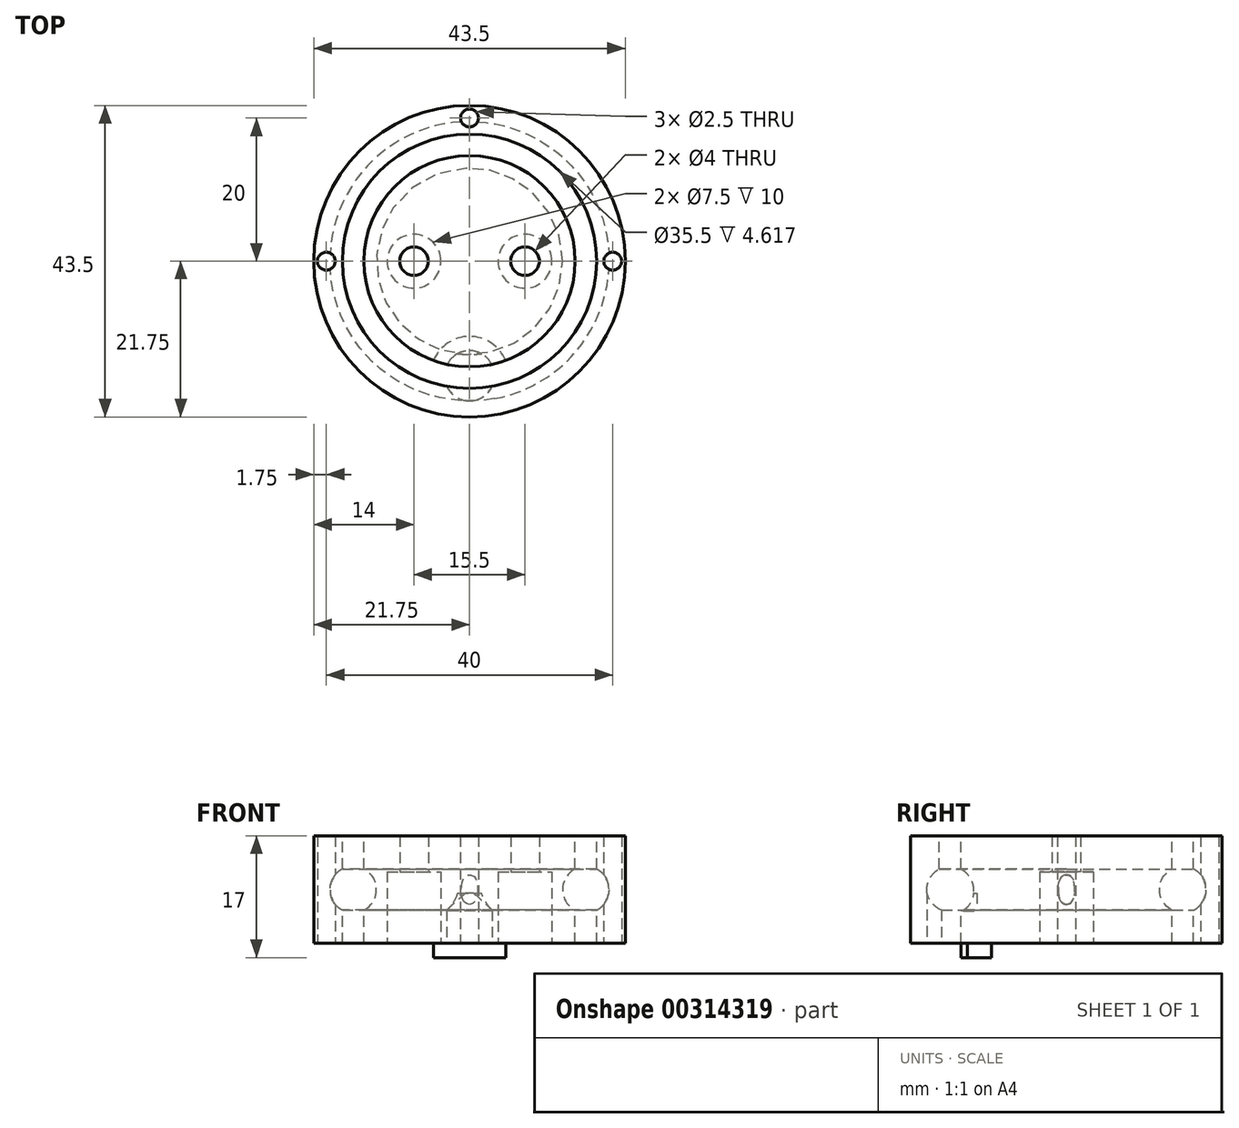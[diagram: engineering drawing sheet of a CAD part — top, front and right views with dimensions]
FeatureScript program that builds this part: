
annotation { "Feature Type Name" : "Feature", "Feature Type Description" : "" }
export const myFeature = defineFeature(function(context is Context, id is Id, definition is map)
    precondition{}
    {
        {
            var Q0;
            Q0=qCreatedBy(makeId("Top.planeOp"),FACE);
            var sketch = newSketch(context, id + "F0", { "sketchPlane" : qUnion([Q0])});
            skCircle(sketch, "E0", {"center": v(0, 0) * mm, "radius": 4 * mm});
            skCircle(sketch, "E1", {"center": v(0, 0) * mm, "radius": 21.75 * mm});
            skCircle(sketch, "E2", {"center": v(0, 0) * mm, "radius": 14.75 * mm});
            skCircle(sketch, "E3", {"center": v(0, 0) * mm, "radius": 17.75 * mm});
            skPoint(sketch, "E4", {"position": v(0, 50.94) * mm});
            skSolve(sketch);
        }
        {
            var Q0;
            Q0=makeQuery(id+"F0.imprint","IMPRINT",FACE,{"disambiguationData":[TD([[makeQuery(id+"F0.imprint","IMPRINT",EDGE,{"derivedFrom":sQuery(id+"F0.wireOp",EDGE,"E1")}),1.0]])]});
            var Q1;
            Q1=makeQuery(id+"F0.imprint","IMPRINT",FACE,{"disambiguationData":[TD([[makeQuery(id+"F0.imprint","IMPRINT",EDGE,{"derivedFrom":sQuery(id+"F0.wireOp",EDGE,"E0")}),-1.0]])]});
            var Q2;
            Q2=makeQuery(id+"F0.imprint","IMPRINT",FACE,{"disambiguationData":[TD([[makeQuery(id+"F0.imprint","IMPRINT",EDGE,{"derivedFrom":sQuery(id+"F0.wireOp",EDGE,"E0")}),1.0]])]});
            extrude(context, id + "F1", {"entities" : qUnion([Q0, Q1, Q2]), "oppositeDirection" : true, "depth" : 15 * mm});
        }
        {
            var Q0;
            Q0=qCreatedBy(makeId("Right.planeOp"),FACE);
            var sketch = newSketch(context, id + "F2", { "sketchPlane" : qUnion([Q0])});
            skLineSegment(sketch, "E5", {"start": v(0, -15) * mm, "end": v(0, 0) * mm});
            skPoint(sketch, "E6", {"position": v(0, -7.5) * mm});
            skSolve(sketch);
        }
        {
            var Q0;
            Q0=makeQuery(id+"F1.opExtrude","CAP_FACE",FACE,{"disambiguationData":[OSD([sQuery(id+"F0.wireOp",EDGE,"E0"),sQuery(id+"F0.wireOp",EDGE,"E2")])],"isStart":false});
            var sketch = newSketch(context, id + "F3", { "sketchPlane" : qUnion([Q0])});
            skPoint(sketch, "E7", {"position": v(0, -14.75) * mm});
            skPoint(sketch, "E8", {"position": v(0, -17.75) * mm});
            skSolve(sketch);
        }
        {
            var Q0;
            Q0=qCreatedBy(makeId("Right.planeOp"),FACE);
            var sketch = newSketch(context, id + "F4", { "sketchPlane" : qUnion([Q0])});
            skCircle(sketch, "E9", {"center": v(16.25, -7.5) * mm, "radius": 3.25 * mm});
            skLineSegment(sketch, "E10", {"start": v(17.75, 0) * mm, "end": v(17.75, -15) * mm});
            skSolve(sketch);
        }
        {
            var Q0;
            Q0=qCreatedBy(makeId("Right.planeOp"),FACE);
            var sketch = newSketch(context, id + "F5", { "sketchPlane" : qUnion([Q0])});
            skLineSegment(sketch, "E11", {"start": v(16.25, -3) * mm, "end": v(16.25, -12) * mm});
            skPoint(sketch, "E12", {"position": v(0, 5) * mm});
            skPoint(sketch, "E13", {"position": v(16.25, -7.5) * mm});
            skArc(sketch, "E14", {"start": v(16.25, -3) * mm, "mid": v(11.75, -7.5) * mm, "end": v(16.25, -12) * mm});
            skSolve(sketch);
        }
        {
            var Q0;
            Q0=makeQuery(id+"F4.imprint","IMPRINT",FACE,{"disambiguationData":[TD([[makeQuery(id+"F4.imprint","IMPRINT",EDGE,{"derivedFrom":sQuery(id+"F4.wireOp",EDGE,"E9")}),1.0]])]});
            var Q1;
            Q1=makeQuery(id+"F1.opExtrude","SWEPT_FACE",FACE,{"disambiguationData":[OSD([sQuery(id+"F0.wireOp",EDGE,"E2")])]});
            revolve(context, id + "F6", {"operationType" : NewBodyOperationType.REMOVE, "entities" : qUnion([Q0]), "axis" : qUnion([Q1]), "revolveType" : RevolveType.FULL, "oppositeDirection" : true});
        }
        {
            var Q0;
            Q0=qCreatedBy(makeId("Top.planeOp"),FACE);
            cPlane(context, id + "F7", {"entities" : qUnion([Q0]), "cplaneType" : CPlaneType.OFFSET, "offset" : 5 * mm, "width" : 150 * mm, "height" : 150 * mm});
        }
        {
            var Q0;
            Q0=makeQuery(id+"F1.opExtrude","CAP_FACE",FACE,{"disambiguationData":[OSD([sQuery(id+"F0.wireOp",EDGE,"E1"),sQuery(id+"F0.wireOp",EDGE,"E3")])],"isStart":false});
            var sketch = newSketch(context, id + "F8", { "sketchPlane" : qUnion([Q0])});
            skCircle(sketch, "E15", {"center": v(0, 16) * mm, "radius": 3.5 * mm});
            skSolve(sketch);
        }
        {
            var Q0;
            Q0=makeQuery(id+"F8.imprint","IMPRINT",FACE,{"disambiguationData":[TD([[makeQuery(id+"F8.imprint","IMPRINT",EDGE,{"derivedFrom":sQuery(id+"F8.wireOp",EDGE,"E15")}),1.0]])]});
            extrude(context, id + "F9", {"entities" : qUnion([Q0]), "operationType" : NewBodyOperationType.REMOVE, "oppositeDirection" : true, "depth" : 7 * mm});
        }
        {
            var Q0;
            Q0=makeQuery(id+"F1.opExtrude","CAP_FACE",FACE,{"disambiguationData":[OSD([sQuery(id+"F0.wireOp",EDGE,"E0"),sQuery(id+"F0.wireOp",EDGE,"E2")])],"isStart":false});
            var sketch = newSketch(context, id + "F10", { "sketchPlane" : qUnion([Q0])});
            skPoint(sketch, "E16", {"position": v(-7.75, 0) * mm});
            skPoint(sketch, "E17", {"position": v(7.75, 0) * mm});
            skCircle(sketch, "E18", {"center": v(-7.75, 0) * mm, "radius": 3.75 * mm});
            skCircle(sketch, "E19", {"center": v(7.75, 0) * mm, "radius": 3.75 * mm});
            skSolve(sketch);
        }
        {
            var Q0;
            Q0=sQuery(id+"F10.wireOp",VERTEX,"E16");
            var Q1;
            Q1=sQuery(id+"F10.wireOp",VERTEX,"E17");
            var Q2;
            Q2=makeQuery(id+"F1.opExtrude","SWEPT_BODY",BODY,{"disambiguationData":[OSD([sQuery(id+"F0.wireOp",EDGE,"E0"),sQuery(id+"F0.wireOp",EDGE,"E2")])]});
            hole(context, id + "F11", {"style" : HoleStyle.SIMPLE, "endStyle" : HoleEndStyle.THROUGH, "holeDiameter" : 4 * mm, "tappedDepth" : 12 * mm, "tapClearance" : 3, "locations" : qUnion([Q0, Q1]), "scope" : qUnion([Q2])});
        }
        {
            var Q0;
            Q0=makeQuery(id+"F10.imprint","IMPRINT",FACE,{"disambiguationData":[TD([[makeQuery(id+"F10.imprint","IMPRINT",EDGE,{"derivedFrom":sQuery(id+"F10.wireOp",EDGE,"E18")}),1.0]])]});
            var Q1;
            Q1=makeQuery(id+"F10.imprint","IMPRINT",FACE,{"disambiguationData":[TD([[makeQuery(id+"F10.imprint","IMPRINT",EDGE,{"derivedFrom":sQuery(id+"F10.wireOp",EDGE,"E19")}),1.0]])]});
            extrude(context, id + "F12", {"entities" : qUnion([Q0, Q1]), "operationType" : NewBodyOperationType.REMOVE, "oppositeDirection" : true, "depth" : 10 * mm});
        }
        {
            var Q0;
            Q0=makeQuery(id+"F1.opExtrude","CAP_FACE",FACE,{"disambiguationData":[OSD([sQuery(id+"F0.wireOp",EDGE,"E1"),sQuery(id+"F0.wireOp",EDGE,"E3")])],"isStart":false});
            var sketch = newSketch(context, id + "F13", { "sketchPlane" : qUnion([Q0])});
            skPoint(sketch, "E20", {"position": v(-20, 0) * mm});
            skPoint(sketch, "E21.1.0", {"position": v(0, -20) * mm});
            skPoint(sketch, "E21.2.0", {"position": v(20, 0) * mm});
            skPoint(sketch, "E21.3.0", {"position": v(0, 20) * mm});
            skPoint(sketch, "E21.center", {"position": v(0, 0) * mm});
            skSolve(sketch);
        }
        {
            var Q0;
            Q0=sQuery(id+"F13.wireOp",VERTEX,"E20");
            var Q1;
            Q1=sQuery(id+"F13.wireOp",VERTEX,"E21.1.0");
            var Q2;
            Q2=sQuery(id+"F13.wireOp",VERTEX,"E21.2.0");
            var Q3;
            Q3=makeQuery(id+"F1.opExtrude","SWEPT_BODY",BODY,{"disambiguationData":[OSD([sQuery(id+"F0.wireOp",EDGE,"E1"),sQuery(id+"F0.wireOp",EDGE,"E3")])]});
            hole(context, id + "F14", {"style" : HoleStyle.SIMPLE, "endStyle" : HoleEndStyle.THROUGH, "holeDiameter" : 2.5 * mm, "tappedDepth" : 12 * mm, "tapClearance" : 3, "locations" : qUnion([Q0, Q1, Q2]), "scope" : qUnion([Q3])});
        }
        {
            var Q0;
            Q0=makeQuery(id+"F1.opExtrude","CAP_FACE",FACE,{"disambiguationData":[OSD([sQuery(id+"F0.wireOp",EDGE,"E2")])],"isStart":false});
            var sketch = newSketch(context, id + "F15", { "sketchPlane" : qUnion([Q0])});
            skCircle(sketch, "E22", {"center": v(0, 0) * mm, "radius": 14.75 * mm});
            skArc(sketch, "E23", {"start": v(-3.12, 14.42) * mm, "mid": v(0, 12.5) * mm, "end": v(3.12, 14.42) * mm});
            skArc(sketch, "E24", {"start": v(-5.04, 13.86) * mm, "mid": v(0, 10.5) * mm, "end": v(5.04, 13.86) * mm});
            skSolve(sketch);
        }
        {
            var Q0;
            {var subQ0=sQuery(id+"F15.wireOp",EDGE,"E23");Q0=makeQuery(id+"F15.imprint","IMPRINT",FACE,{"disambiguationData":[TD([[makeQuery(id+"F15.imprint","IMPRINT",EDGE,{"derivedFrom":subQ0}),1.0]])]});}
            var Q1;
            {var subQ0=sQuery(id+"F15.wireOp",EDGE,"E23");Q1=makeQuery(id+"F15.imprint","IMPRINT",FACE,{"disambiguationData":[TD([[makeQuery(id+"F15.imprint","IMPRINT",EDGE,{"derivedFrom":subQ0}),-1.0]])]});}
            extrude(context, id + "F16", {"entities" : qUnion([Q0, Q1]), "depth" : 2 * mm});
        }
        {
            var Q0;
            {var subQ0=sQuery(id+"F15.wireOp",EDGE,"E23");Q0=makeQuery(id+"F15.imprint","IMPRINT",FACE,{"disambiguationData":[TD([[makeQuery(id+"F15.imprint","IMPRINT",EDGE,{"derivedFrom":subQ0}),1.0]])]});}
            extrude(context, id + "F17", {"entities" : qUnion([Q0]), "operationType" : NewBodyOperationType.ADD, "oppositeDirection" : true, "depth" : 4.5 * mm});
        }
    });
